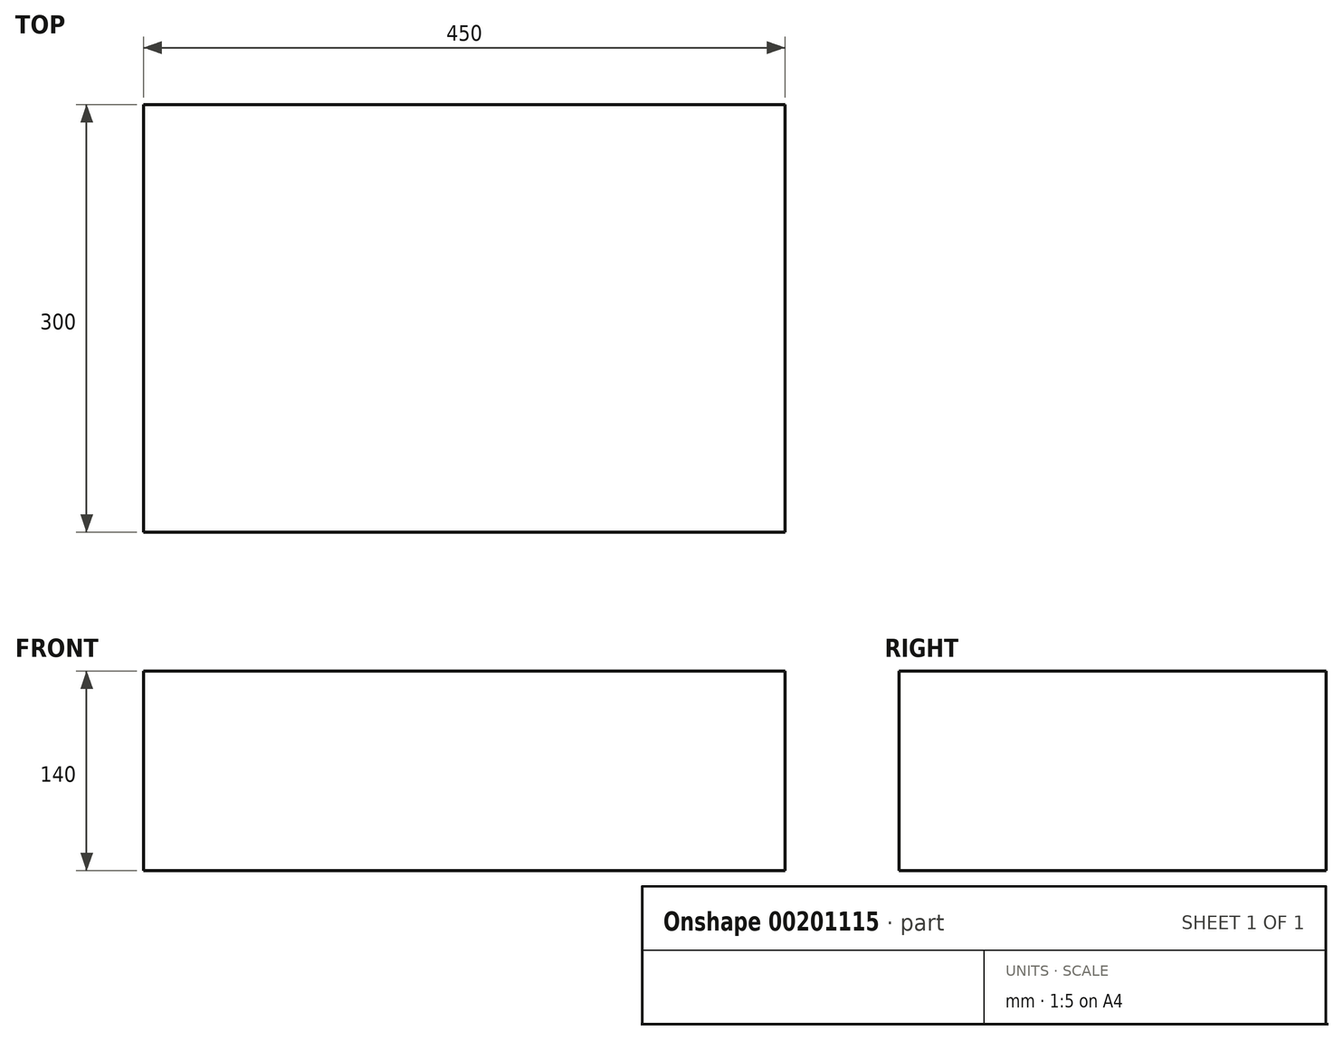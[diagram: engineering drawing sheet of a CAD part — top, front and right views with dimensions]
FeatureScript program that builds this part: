
annotation { "Feature Type Name" : "Feature", "Feature Type Description" : "" }
export const myFeature = defineFeature(function(context is Context, id is Id, definition is map)
    precondition{}
    {
        {
            var Q0;
            Q0=qCreatedBy(makeId("Top.planeOp"),FACE);
            var sketch = newSketch(context, id + "F0", { "sketchPlane" : qUnion([Q0])});
            skLineSegment(sketch, "E0.bottom", {"start": v(225, -150) * mm, "end": v(-225, -150) * mm});
            skLineSegment(sketch, "E0.top", {"start": v(225, 150) * mm, "end": v(-225, 150) * mm});
            skLineSegment(sketch, "E0.left", {"start": v(225, -150) * mm, "end": v(225, 150) * mm});
            skLineSegment(sketch, "E0.right", {"start": v(-225, -150) * mm, "end": v(-225, 150) * mm});
            skPoint(sketch, "E0.middle", {"position": v(0, 0) * mm});
            skSolve(sketch);
        }
        {
            var Q0;
            Q0 = qSketchRegion(id + "F0", true);
            extrude(context, id + "F1", {"entities" : qUnion([Q0]), "depth" : 140 * mm});
        }
    });
